# Revit family: Обратный клапан 2623
name_source: partatom
category: Rohrzubehör
units: mm (PartAtom-declared; Revit-internal decimal feet)

## family parameters
Arbeitsebenenbasiert = Nein
Beim Laden mit Abzugskörper schneiden = Nein
Bemaßung runder Anschluss = Durchmesser verwenden
Gemeinsam genutzt = Nein
Immer vertikal = Ja
OmniClass-Nummer = 23.65.55.14
OmniClass-Titel = Valves for Liquid Services
Teiletyp = Unterbricht

## types (1)
- Обратный клапан 2623
    H02 = 2 mm  [stored 0.00656168 ft]
    Hersteller = HERZ Armaturen Ges.m.b.H.
    R01 = 9 mm  [stored 0.0295276 ft]
    S03 = 10 mm  [stored 0.0328084 ft]
    SCTWCODE = 04;14;02
    SCTWSEQ = FW;SBT_TYP_FW="108";2
    SC_NennweiteBerechnet = 0
    URL = www.herz-armaturen.ru
    Vorgabe-Ansicht = 0 mm  [stored 0 ft]
    W01 = 45.00°
    Заглушка = латунь
    Корпус = штампованная латунь согласно EN 12420
    Макс. рабочая температура = 95 °C
    Макс. рабочее давление = 1600000.0 Pa
    Мин. рабочая температура = -10 °C
    Мин. рабочая температура (вода) = 1 °C
    Накидная гайка = штампованная латунь
    Область применения = Может использоваться в системах отопления, в инженерных системах и сооружениях для предотвращения движения потока в обратном направлении.
Это изделие может использоваться с различными средами, при этом жидкости должны быть чистыми.
Клапан может монтироваться в любом положении.
Направление движения потока указано стрелкой на корпусе клапана.
Обратный клапан подпружинен с помощью осевой направляющей и может работать как при высоком, так и при низком давлении.
В корпусе есть два отверстия для замеров, в каждое из которых установлены заглушки 1/4".
    Обратный клапан = POM (корпус),  NBR (O-Ring), нержавеющая сталь AISI 302 (пружина)
    Примечание = В соответствии со статьей 33 Регламента REACH (Registration; Evaluation; Authorisation; Restriction of Chemicals) (EC № 1907/2006) мы обязаны указать, что свинец внесен в список SVHC (Substances of Very High Concern - вещества очень высокой важности) и весовой процент свинца во всех латунных компонентах заводского изготовления в наших изделиях, превышает 0,1 % (w/w) (CAS: 7439-92-1 / EINECS: 231-100-4).
Поскольку свинец является легирующим компонентом сплава, прямое негативное влияние исключается, и поэтому дополнительной информации о безопасном использовании не требуется.
    Резьба = согласно ISO 228
    Среда = чистая вода
    Уплотнение = EPDM

note: [stored X ft] marks values corroborated as IEEE doubles in the binary element streams (Revit-internal decimal feet)
